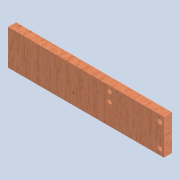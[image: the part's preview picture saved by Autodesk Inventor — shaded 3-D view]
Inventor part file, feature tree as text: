
AUTODESK INVENTOR PART (.ipt)
format: ipt  version: 2020 (Build 240168000, 168)  size: 114,688 bytes
history: native  units: mm
features: sketch x3, hole x2, reference x2, other x2, extrude x1
ambient origin geometry x8: Origin, YZ Plane, XZ Plane, XY Plane, X Axis, Y Axis, Z Axis, Center Point
bodies: Solid1 (feature_tree)
feature tree (10):
  extrude  "Extrusion1"  Depth=35.0mm
  hole  "Hole1"  [1 undecoded]
  hole  "Hole2"  [1 undecoded]
  sketch  "Sketch1"  dims[d0=155.0mm d1=35.0mm]
  sketch  "Sketch4"  dims[d2=8.0mm d3=0.0mm d19=4.0mm]
  sketch  "Sketch5"  dims[d20=6.0mm d21=4.5mm d22=6.0mm d23=4.0mm d24=2.0mm d25=90.0deg d26=8.0mm d27=20.594885mm d28=4.0mm d29=6.0mm d30=4.0mm d31=2.0mm d32=90.0deg d33=8.0mm d34=20.594885mm]
  reference  "Reference1"
  reference  "Reference2"
  other  "0005-10-04 Y axis and extruder.iam"
  other  "0005-10-010.ipt:15"
note: 2 required parameter values undecoded (feature->parameter linkage not recoverable at this tier; creation-order binding heuristic only, values carry confidence <= 0.55)
